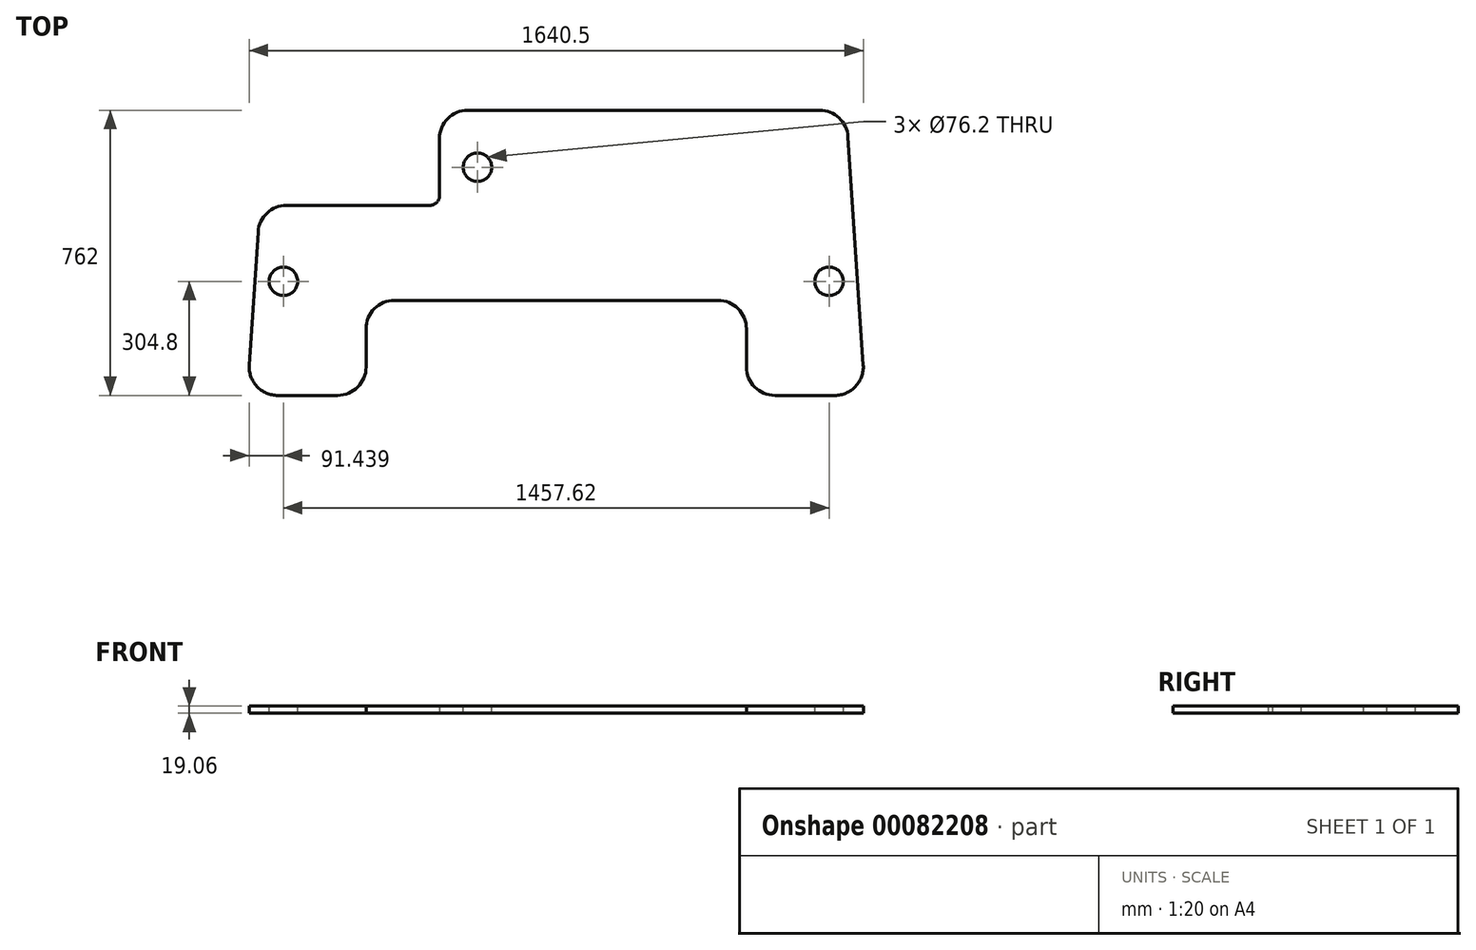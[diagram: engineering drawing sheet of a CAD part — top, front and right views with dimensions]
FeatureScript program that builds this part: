
annotation { "Feature Type Name" : "Feature", "Feature Type Description" : "" }
export const myFeature = defineFeature(function(context is Context, id is Id, definition is map)
    precondition{}
    {
        {
            var Q0;
            Q0=qCreatedBy(makeId("Top.planeOp"),FACE);
            var sketch = newSketch(context, id + "F0", { "sketchPlane" : qUnion([Q0])});
            skLineSegment(sketch, "E0.bottom", {"start": v(-235.88, 381) * mm, "end": v(703.41, 381) * mm});
            skLineSegment(sketch, "E0.top", {"start": v(-744.05, -381) * mm, "end": v(-584.2, -381) * mm});
            skLineSegment(sketch, "E1", {"start": v(820.08, -299.73) * mm, "end": v(779.44, 309.87) * mm});
            skLineSegment(sketch, "E2", {"start": v(-820.08, -299.73) * mm, "end": v(-796.38, 55.87) * mm});
            skLineSegment(sketch, "E3.top", {"start": v(-431.8, -127) * mm, "end": v(431.8, -127) * mm});
            skLineSegment(sketch, "E3.left", {"start": v(-508, -304.8) * mm, "end": v(-508, -203.2) * mm});
            skLineSegment(sketch, "E3.right", {"start": v(508, -304.8) * mm, "end": v(508, -203.2) * mm});
            skPoint(sketch, "E0.left.start.orphan", {"position": v(-825.5, 381) * mm});
            skPoint(sketch, "E4.orphan", {"position": v(825.5, 381) * mm});
            skLineSegment(sketch, "E5.trimOffspring", {"start": v(584.2, -381) * mm, "end": v(744.05, -381) * mm});
            skPoint(sketch, "E6.visualSharp", {"position": v(-508, -127) * mm});
            skArc(sketch, "E6.filletArc", {"start": v(-431.8, -127) * mm, "mid": v(-485.68, -149.32) * mm, "end": v(-508, -203.2) * mm});
            skPoint(sketch, "E7.visualSharp", {"position": v(508, -127) * mm});
            skArc(sketch, "E7.filletArc", {"start": v(508, -203.2) * mm, "mid": v(485.68, -149.32) * mm, "end": v(431.8, -127) * mm});
            skPoint(sketch, "E8.visualSharp", {"position": v(508, -381) * mm});
            skArc(sketch, "E8.filletArc", {"start": v(508, -304.8) * mm, "mid": v(530.32, -358.68) * mm, "end": v(584.2, -381) * mm});
            skPoint(sketch, "E9.visualSharp", {"position": v(825.5, -381) * mm});
            skArc(sketch, "E9.filletArc", {"start": v(744.05, -381) * mm, "mid": v(799.7, -356.86) * mm, "end": v(820.08, -299.73) * mm});
            skPoint(sketch, "E10.visualSharp", {"position": v(774.7, 381) * mm});
            skArc(sketch, "E10.filletArc", {"start": v(779.44, 309.87) * mm, "mid": v(755.47, 360.44) * mm, "end": v(703.41, 381) * mm});
            skPoint(sketch, "E11.visualSharp", {"position": v(-508, -381) * mm});
            skArc(sketch, "E11.filletArc", {"start": v(-584.2, -381) * mm, "mid": v(-530.32, -358.68) * mm, "end": v(-508, -304.8) * mm});
            skPoint(sketch, "E12.visualSharp", {"position": v(-825.5, -381) * mm});
            skArc(sketch, "E12.filletArc", {"start": v(-820.08, -299.73) * mm, "mid": v(-799.7, -356.86) * mm, "end": v(-744.05, -381) * mm});
            skLineSegment(sketch, "E13.top", {"start": v(-337.48, 127) * mm, "end": v(-720.34, 127) * mm});
            skLineSegment(sketch, "E13.left", {"start": v(-312.08, 304.8) * mm, "end": v(-312.08, 152.4) * mm});
            skPoint(sketch, "E13.bottom.start.orphan", {"position": v(-774.7, 381) * mm});
            skPoint(sketch, "E14.visualSharp", {"position": v(-791.63, 127) * mm});
            skArc(sketch, "E14.filletArc", {"start": v(-720.34, 127) * mm, "mid": v(-772.4, 106.44) * mm, "end": v(-796.38, 55.87) * mm});
            skPoint(sketch, "E15.visualSharp", {"position": v(-312.08, 381) * mm});
            skArc(sketch, "E15.filletArc", {"start": v(-235.88, 381) * mm, "mid": v(-289.76, 358.68) * mm, "end": v(-312.08, 304.8) * mm});
            skPoint(sketch, "E16.visualSharp", {"position": v(-312.08, 127) * mm});
            skArc(sketch, "E16.filletArc", {"start": v(-337.48, 127) * mm, "mid": v(-319.52, 134.44) * mm, "end": v(-312.08, 152.4) * mm});
            skSolve(sketch);
        }
        {
            var Q0;
            Q0=makeQuery(id+"F0.imprint","IMPRINT",FACE,{"disambiguationData":[TD([[makeQuery(id+"F0.imprint","IMPRINT",EDGE,{"derivedFrom":sQuery(id+"F0.wireOp",EDGE,"E0.bottom")}),-1.0]])]});
            extrude(context, id + "F1", {"entities" : qUnion([Q0]), "endBound" : BoundingType.SYMMETRIC, "depth" : 19.05 * mm});
        }
        {
            var Q0;
            Q0=makeQuery(id+"F1.opExtrude","CAP_FACE",FACE,{"disambiguationData":[OSD([sQuery(id+"F0.wireOp",EDGE,"E0.bottom"),sQuery(id+"F0.wireOp",EDGE,"E0.top"),sQuery(id+"F0.wireOp",EDGE,"E1"),sQuery(id+"F0.wireOp",EDGE,"E2"),sQuery(id+"F0.wireOp",EDGE,"E3.top"),sQuery(id+"F0.wireOp",EDGE,"E3.left"),sQuery(id+"F0.wireOp",EDGE,"E3.right"),sQuery(id+"F0.wireOp",EDGE,"E5.trimOffspring"),sQuery(id+"F0.wireOp",EDGE,"E6.filletArc"),sQuery(id+"F0.wireOp",EDGE,"E7.filletArc"),sQuery(id+"F0.wireOp",EDGE,"E8.filletArc"),sQuery(id+"F0.wireOp",EDGE,"E9.filletArc"),sQuery(id+"F0.wireOp",EDGE,"E10.filletArc"),sQuery(id+"F0.wireOp",EDGE,"E11.filletArc"),sQuery(id+"F0.wireOp",EDGE,"E12.filletArc"),sQuery(id+"F0.wireOp",EDGE,"E13.top"),sQuery(id+"F0.wireOp",EDGE,"E13.left"),sQuery(id+"F0.wireOp",EDGE,"E14.filletArc"),sQuery(id+"F0.wireOp",EDGE,"E15.filletArc"),sQuery(id+"F0.wireOp",EDGE,"E16.filletArc")])],"isStart":false});
            var sketch = newSketch(context, id + "F2", { "sketchPlane" : qUnion([Q0])});
            skCircle(sketch, "E17", {"center": v(-210.48, 228.6) * mm, "radius": 38.1 * mm});
            skSolve(sketch);
        }
        {
            var Q0;
            Q0 = qSketchRegion(id + "F2", true);
            extrude(context, id + "F3", {"entities" : qUnion([Q0]), "operationType" : NewBodyOperationType.REMOVE, "endBound" : BoundingType.THROUGH_ALL, "oppositeDirection" : true, "depth" : 25.4 * mm});
        }
        {
            var Q0;
            Q0=makeQuery(id+"F1.opExtrude","CAP_FACE",FACE,{"disambiguationData":[OSD([sQuery(id+"F0.wireOp",EDGE,"E0.bottom"),sQuery(id+"F0.wireOp",EDGE,"E0.top"),sQuery(id+"F0.wireOp",EDGE,"E1"),sQuery(id+"F0.wireOp",EDGE,"E2"),sQuery(id+"F0.wireOp",EDGE,"E3.top"),sQuery(id+"F0.wireOp",EDGE,"E3.left"),sQuery(id+"F0.wireOp",EDGE,"E3.right"),sQuery(id+"F0.wireOp",EDGE,"E5.trimOffspring"),sQuery(id+"F0.wireOp",EDGE,"E6.filletArc"),sQuery(id+"F0.wireOp",EDGE,"E7.filletArc"),sQuery(id+"F0.wireOp",EDGE,"E8.filletArc"),sQuery(id+"F0.wireOp",EDGE,"E9.filletArc"),sQuery(id+"F0.wireOp",EDGE,"E10.filletArc"),sQuery(id+"F0.wireOp",EDGE,"E11.filletArc"),sQuery(id+"F0.wireOp",EDGE,"E12.filletArc"),sQuery(id+"F0.wireOp",EDGE,"E13.top"),sQuery(id+"F0.wireOp",EDGE,"E13.left"),sQuery(id+"F0.wireOp",EDGE,"E14.filletArc"),sQuery(id+"F0.wireOp",EDGE,"E15.filletArc"),sQuery(id+"F0.wireOp",EDGE,"E16.filletArc")])],"isStart":false});
            var sketch = newSketch(context, id + "F4", { "sketchPlane" : qUnion([Q0])});
            skCircle(sketch, "E18", {"center": v(-728.81, -76.2) * mm, "radius": 38.1 * mm});
            skSolve(sketch);
        }
        {
            var Q0;
            Q0 = qSketchRegion(id + "F4", true);
            extrude(context, id + "F5", {"entities" : qUnion([Q0]), "operationType" : NewBodyOperationType.REMOVE, "endBound" : BoundingType.THROUGH_ALL, "oppositeDirection" : true, "depth" : 25.4 * mm});
        }
        {
            var Q0;
            Q0=makeQuery(id+"F1.opExtrude","CAP_FACE",FACE,{"disambiguationData":[OSD([sQuery(id+"F0.wireOp",EDGE,"E0.bottom"),sQuery(id+"F0.wireOp",EDGE,"E0.top"),sQuery(id+"F0.wireOp",EDGE,"E1"),sQuery(id+"F0.wireOp",EDGE,"E2"),sQuery(id+"F0.wireOp",EDGE,"E3.top"),sQuery(id+"F0.wireOp",EDGE,"E3.left"),sQuery(id+"F0.wireOp",EDGE,"E3.right"),sQuery(id+"F0.wireOp",EDGE,"E5.trimOffspring"),sQuery(id+"F0.wireOp",EDGE,"E6.filletArc"),sQuery(id+"F0.wireOp",EDGE,"E7.filletArc"),sQuery(id+"F0.wireOp",EDGE,"E8.filletArc"),sQuery(id+"F0.wireOp",EDGE,"E9.filletArc"),sQuery(id+"F0.wireOp",EDGE,"E10.filletArc"),sQuery(id+"F0.wireOp",EDGE,"E11.filletArc"),sQuery(id+"F0.wireOp",EDGE,"E12.filletArc"),sQuery(id+"F0.wireOp",EDGE,"E13.top"),sQuery(id+"F0.wireOp",EDGE,"E13.left"),sQuery(id+"F0.wireOp",EDGE,"E14.filletArc"),sQuery(id+"F0.wireOp",EDGE,"E15.filletArc"),sQuery(id+"F0.wireOp",EDGE,"E16.filletArc")])],"isStart":false});
            var sketch = newSketch(context, id + "F6", { "sketchPlane" : qUnion([Q0])});
            skCircle(sketch, "E19", {"center": v(728.81, -76.2) * mm, "radius": 38.1 * mm});
            skSolve(sketch);
        }
        {
            var Q0;
            Q0 = qSketchRegion(id + "F6", true);
            extrude(context, id + "F7", {"entities" : qUnion([Q0]), "operationType" : NewBodyOperationType.REMOVE, "oppositeDirection" : true, "depth" : 25.4 * mm});
        }
    });
